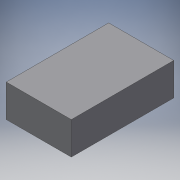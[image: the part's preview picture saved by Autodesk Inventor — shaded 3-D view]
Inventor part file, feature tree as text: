
AUTODESK INVENTOR PART (.ipt)
format: ipt  version: 2019.4 (Build 234330000, 330)  size: 153,088 bytes
history: native  units: mm
features: sketch x4, extrude x3, hole x1, pattern_linear x1, mirror x1, fillet x1
ambient origin geometry x8: Origin, YZ Plane, XZ Plane, XY Plane, X Axis, Y Axis, Z Axis, Center Point
bodies: Solid1 (feature_tree)
feature tree (11):
  extrude  "Extrusion1"  Depth=30.0mm
  hole  "Hole1"  [1 undecoded]
  pattern_linear  "Rectangular Pattern1"  Count1=2 Spacing1=10.0mm
  mirror  "Mirror1"
  extrude  "Extrusion2"  Depth=10.0mm
  extrude  "Extrusion3"  Depth=26.0mm
  fillet  "Fillet1"  Radius=30.0mm
  sketch  "Sketch1"  dims[d0=31.5mm d1=30.0mm]
  sketch  "Sketch2"  dims[d2=8.0mm d3=0.0mm d4=3.0mm]
  sketch  "Sketch3"  dims[d5=8.0mm]
  sketch  "Sketch4"  dims[d6=4.0mm d7=3.88mm d8=15.0mm d9=4.34mm d10=2.0mm d11=1.22173mm d12=7.0mm d13=0.0mm d14=20.0mm d16=10.0mm d17=20.0mm d19=10.0mm d20=26.0mm d21=30.0mm d22=5.0mm d23=0.0mm d24=80.0mm d25=6.0mm d26=0.0mm d27=2.0mm]
note: 1 required parameter value undecoded (feature->parameter linkage not recoverable at this tier; creation-order binding heuristic only, values carry confidence <= 0.55)
